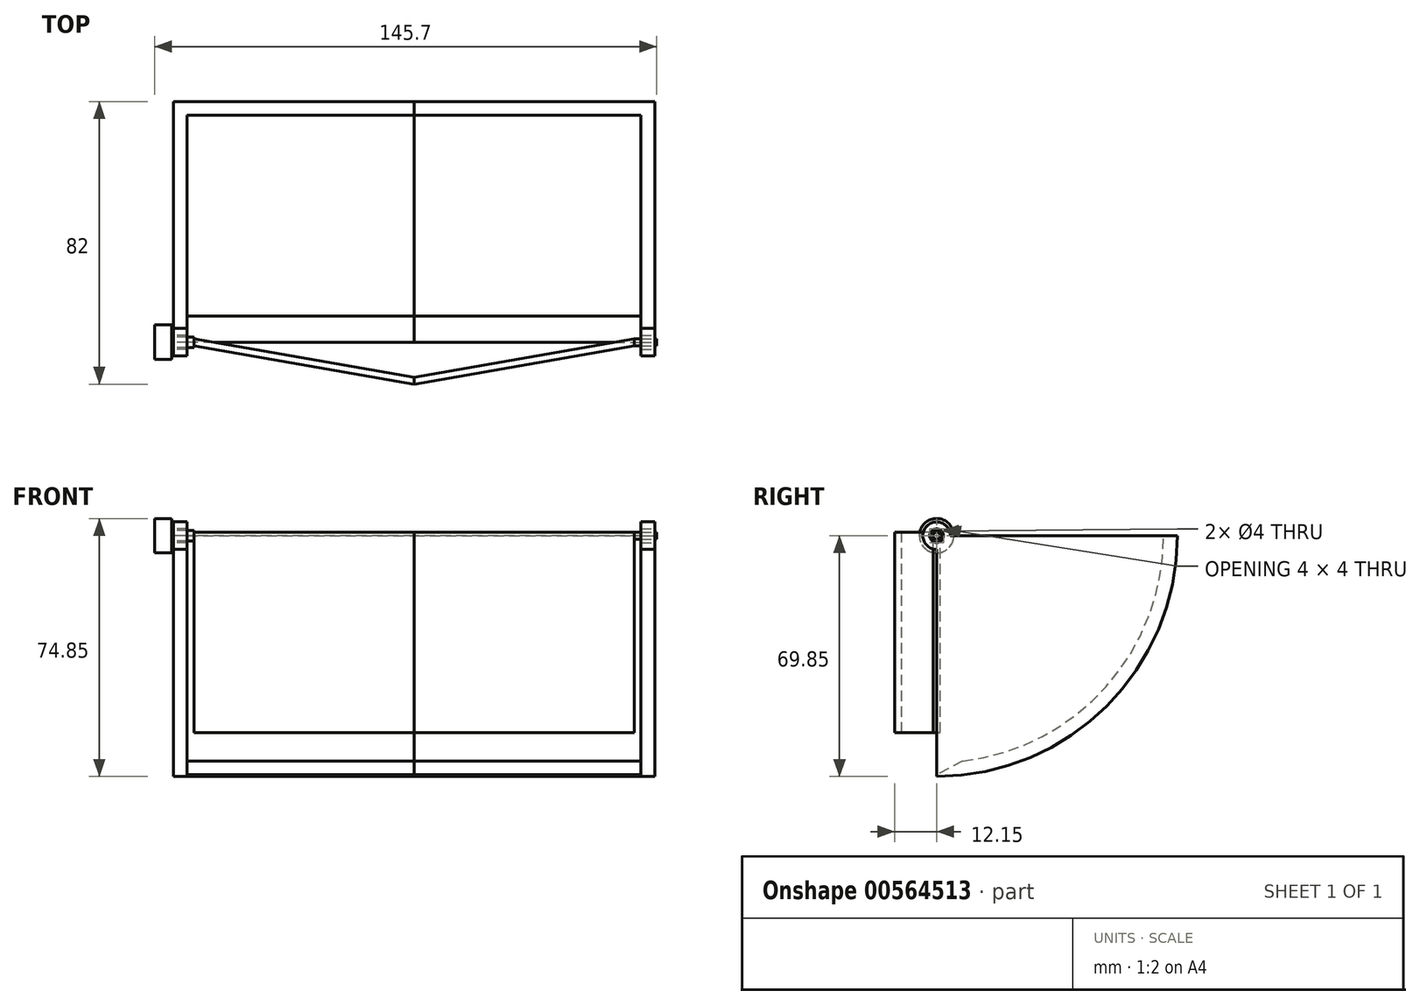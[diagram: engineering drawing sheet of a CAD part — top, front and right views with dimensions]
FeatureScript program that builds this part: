
annotation { "Feature Type Name" : "Feature", "Feature Type Description" : "" }
export const myFeature = defineFeature(function(context is Context, id is Id, definition is map)
    precondition{}
    {
        {
            var Q0;
            Q0=qCreatedBy(makeId("Top.planeOp"),FACE);
            var sketch = newSketch(context, id + "F0", { "sketchPlane" : qUnion([Q0])});
            skLineSegment(sketch, "E0", {"start": v(0, 0) * mm, "end": v(0, -69.85) * mm});
            skLineSegment(sketch, "E1", {"start": v(0, -69.85) * mm, "end": v(4, -69.85) * mm});
            skLineSegment(sketch, "E2", {"start": v(4, -69.85) * mm, "end": v(4, -4) * mm});
            skLineSegment(sketch, "E3", {"start": v(4, -4) * mm, "end": v(69.85, -4) * mm});
            skLineSegment(sketch, "E4", {"start": v(69.85, 0) * mm, "end": v(0, 0) * mm});
            skLineSegment(sketch, "E5", {"start": v(-28.64, -69.85) * mm, "end": v(113.81, -69.85) * mm, "construction": true});
            skLineSegment(sketch, "E6", {"start": v(69.85, 0) * mm, "end": v(69.85, -4) * mm});
            skSolve(sketch);
        }
        {
            var Q0;
            Q0=makeQuery(id+"F0.imprint","IMPRINT",FACE,{"disambiguationData":[TD([[makeQuery(id+"F0.imprint","IMPRINT",EDGE,{"derivedFrom":sQuery(id+"F0.wireOp",EDGE,"E0")}),1.0]])]});
            var Q1;
            Q1=sQuery(id+"F0.wireOp",EDGE,"E4");
            var Q2;
            Q2=sQuery(id+"F0.wireOp",EDGE,"E3");
            var Q3;
            Q3=sQuery(id+"F0.wireOp",EDGE,"E5");
            revolve(context, id + "F1", {"entities" : qUnion([Q0]), "surfaceEntities" : qUnion([Q1, Q2]), "axis" : qUnion([Q3]), "revolveType" : RevolveType.ONE_DIRECTION, "oppositeDirection" : true, "angle" : 90 * degree});
        }
        {
            var Q0;
            Q0=makeQuery(id+"F1.opRevolve","CAP_EDGE",EDGE,{"disambiguationData":[OSD([sQuery(id+"F0.wireOp",EDGE,"E3")])],"isStart":false});
            chamfer(context, id + "F2", {"entities" : qUnion([Q0]), "chamferType" : ChamferType.TWO_OFFSETS, "width1" : 8 * mm, "oppositeDirection" : false, "width2" : 4 * mm, "tangentPropagation" : true});
        }
        {
            var Q0;
            Q0=makeQuery(id+"F1.opRevolve","SWEPT_FACE",FACE,{"disambiguationData":[OSD([sQuery(id+"F0.wireOp",EDGE,"E0")])]});
            var sketch = newSketch(context, id + "F3", { "sketchPlane" : qUnion([Q0])});
            skCircle(sketch, "E7", {"center": v(69.85, 0) * mm, "radius": 4 * mm});
            skSolve(sketch);
        }
        {
            var Q0;
            Q0 = qSketchRegion(id + "F3", true);
            extrude(context, id + "F4", {"entities" : qUnion([Q0]), "operationType" : NewBodyOperationType.ADD, "oppositeDirection" : true, "depth" : 4 * mm, "offsetDistance" : 25 * mm});
        }
        {
            var Q0;
            Q0=makeQuery(id+"F4.boolean.opBoolean","MERGE",FACE,{"derivedFrom":[makeQuery(id+"F1.opRevolve","SWEPT_FACE",FACE,{"disambiguationData":[OSD([sQuery(id+"F0.wireOp",EDGE,"E0")])]}),makeQuery(id+"F4.opExtrude","CAP_FACE",FACE,{"disambiguationData":[OSD([sQuery(id+"F3.wireOp",EDGE,"E7")])],"isStart":true})]});
            var sketch = newSketch(context, id + "F5", { "sketchPlane" : qUnion([Q0])});
            skCircle(sketch, "E8", {"center": v(69.85, 0) * mm, "radius": 2 * mm});
            skSolve(sketch);
        }
        {
            var Q0;
            Q0 = qSketchRegion(id + "F5", true);
            extrude(context, id + "F6", {"entities" : qUnion([Q0]), "operationType" : NewBodyOperationType.REMOVE, "oppositeDirection" : true, "depth" : 25 * mm, "offsetDistance" : 25 * mm});
        }
        {
            var Q0;
            Q0=makeQuery(id+"F4.boolean.opBoolean","MERGE",FACE,{"derivedFrom":[makeQuery(id+"F1.opRevolve","SWEPT_FACE",FACE,{"disambiguationData":[OSD([sQuery(id+"F0.wireOp",EDGE,"E0")])]}),makeQuery(id+"F4.opExtrude","CAP_FACE",FACE,{"disambiguationData":[OSD([sQuery(id+"F3.wireOp",EDGE,"E7")])],"isStart":true})]});
            var sketch = newSketch(context, id + "F7", { "sketchPlane" : qUnion([Q0])});
            skCircle(sketch, "E9", {"center": v(69.85, 0) * mm, "radius": 1 * mm});
            skSolve(sketch);
        }
        {
            var Q0;
            Q0 = qSketchRegion(id + "F7", true);
            extrude(context, id + "F8", {"entities" : qUnion([Q0]), "oppositeDirection" : true, "depth" : 6 * mm, "offsetDistance" : 25 * mm, "hasSecondDirection" : true, "secondDirectionOppositeDirection" : false, "secondDirectionDepth" : .5 * mm});
        }
        {
            var Q0;
            Q0=makeQuery(id+"F1.opRevolve","CAP_FACE",FACE,{"disambiguationData":[OSD([sQuery(id+"F0.wireOp",EDGE,"E0"),sQuery(id+"F0.wireOp",EDGE,"E1"),sQuery(id+"F0.wireOp",EDGE,"E2"),sQuery(id+"F0.wireOp",EDGE,"E3"),sQuery(id+"F0.wireOp",EDGE,"E4"),sQuery(id+"F0.wireOp",EDGE,"E6")])],"isStart":true});
            var sketch = newSketch(context, id + "F9", { "sketchPlane" : qUnion([Q0])});
            skLineSegment(sketch, "E10", {"start": v(6, -65.85) * mm, "end": v(6, -68.85) * mm});
            skLineSegment(sketch, "E11", {"start": v(6, -68.85) * mm, "end": v(6, -70.85) * mm});
            skLineSegment(sketch, "E12", {"start": v(6, -70.85) * mm, "end": v(69.85, -82) * mm});
            skLineSegment(sketch, "E13", {"start": v(69.85, -82) * mm, "end": v(69.85, -80) * mm});
            skLineSegment(sketch, "E14", {"start": v(69.85, -80) * mm, "end": v(6, -68.85) * mm});
            skSolve(sketch);
        }
        {
            var Q0;
            Q0 = qSketchRegion(id + "F9", true);
            extrude(context, id + "F10", {"entities" : qUnion([Q0]), "operationType" : NewBodyOperationType.ADD, "oppositeDirection" : true, "depth" : 57.15 * mm, "offsetDistance" : 25 * mm, "hasSecondDirection" : true, "secondDirectionOppositeDirection" : false, "secondDirectionDepth" : 1 * mm});
        }
        {
            var Q0;
            Q0=makeQuery(id+"F1.opRevolve","SWEPT_BODY",BODY,{"disambiguationData":[OSD([sQuery(id+"F0.wireOp",EDGE,"E0"),sQuery(id+"F0.wireOp",EDGE,"E1"),sQuery(id+"F0.wireOp",EDGE,"E2"),sQuery(id+"F0.wireOp",EDGE,"E3"),sQuery(id+"F0.wireOp",EDGE,"E4"),sQuery(id+"F0.wireOp",EDGE,"E6")])]});
            var Q1;
            Q1=makeQuery(id+"F8.opExtrude","SWEPT_BODY",BODY,{"disambiguationData":[OSD([sQuery(id+"F7.wireOp",EDGE,"E9")])]});
            var Q2;
            Q2=makeQuery(id+"F1.opRevolve","SWEPT_FACE",FACE,{"disambiguationData":[OSD([sQuery(id+"F0.wireOp",EDGE,"E6")])]});
            mirror(context, id + "F11", {"entities" : qUnion([Q0, Q1]), "mirrorPlane" : qUnion([Q2])});
        }
        {
            var Q0;
            Q0=makeQuery(id+"F8.opExtrude","CAP_FACE",FACE,{"disambiguationData":[OSD([sQuery(id+"F7.wireOp",EDGE,"E9")])],"isStart":true});
            var sketch = newSketch(context, id + "F12", { "sketchPlane" : qUnion([Q0])});
            skCircle(sketch, "E15", {"center": v(69.85, 0) * mm, "radius": 5 * mm});
            skSolve(sketch);
        }
        {
            var Q0;
            Q0 = qSketchRegion(id + "F12", true);
            extrude(context, id + "F13", {"entities" : qUnion([Q0]), "operationType" : NewBodyOperationType.ADD, "depth" : 5 * mm, "offsetDistance" : 25 * mm});
        }
        {
            var Q0;
            Q0=makeQuery(id+"F4.boolean.opBoolean","MERGE",FACE,{"derivedFrom":[makeQuery(id+"F1.opRevolve","SWEPT_FACE",FACE,{"disambiguationData":[OSD([sQuery(id+"F0.wireOp",EDGE,"E0")])]}),makeQuery(id+"F4.opExtrude","CAP_FACE",FACE,{"disambiguationData":[OSD([sQuery(id+"F3.wireOp",EDGE,"E7")])],"isStart":true})]});
            var sketch = newSketch(context, id + "F14", { "sketchPlane" : qUnion([Q0])});
            skCircle(sketch, "E16", {"center": v(69.85, 0) * mm, "radius": 1.5 * mm});
            skSolve(sketch);
        }
        {
            var Q0;
            Q0 = qSketchRegion(id + "F14", true);
            extrude(context, id + "F15", {"entities" : qUnion([Q0]), "operationType" : NewBodyOperationType.ADD, "oppositeDirection" : true, "depth" : 6 * mm, "offsetDistance" : 25 * mm, "hasSecondDirection" : true, "secondDirectionOppositeDirection" : false, "secondDirectionDepth" : 1 * mm});
        }
    });
